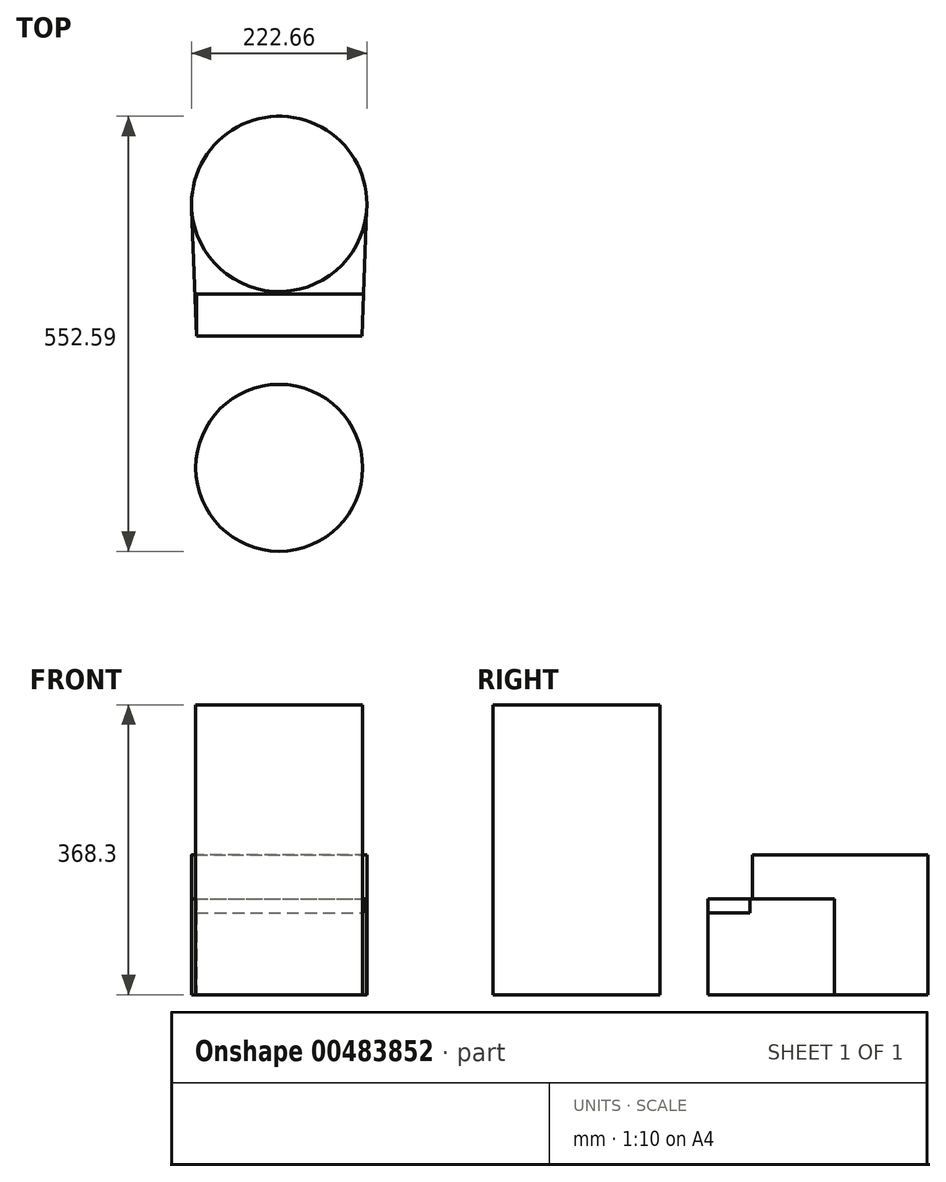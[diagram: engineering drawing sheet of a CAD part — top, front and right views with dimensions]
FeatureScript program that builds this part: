
annotation { "Feature Type Name" : "Feature", "Feature Type Description" : "" }
export const myFeature = defineFeature(function(context is Context, id is Id, definition is map)
    precondition{}
    {
        {
            var Q0;
            Q0=qCreatedBy(makeId("Top.planeOp"),FACE);
            var sketch = newSketch(context, id + "F0", { "sketchPlane" : qUnion([Q0])});
            skCircle(sketch, "E0", {"center": v(0, 168.12) * mm, "radius": 111.33 * mm});
            skCircle(sketch, "E1", {"center": v(0, -167.11) * mm, "radius": 106.03 * mm});
            skLineSegment(sketch, "E2", {"start": v(-111.1, 160.8) * mm, "end": v(-100.24, -132.56) * mm});
            skLineSegment(sketch, "E3", {"start": v(-111.1, 160.8) * mm, "end": v(111.1, 160.8) * mm});
            skLineSegment(sketch, "E4", {"start": v(111.1, 160.8) * mm, "end": v(100.24, -132.56) * mm});
            skLineSegment(sketch, "E5", {"start": v(-100.24, -132.56) * mm, "end": v(100.24, -132.56) * mm});
            skLineSegment(sketch, "E6", {"start": v(0, 168.12) * mm, "end": v(0, -167.11) * mm});
            skLineSegment(sketch, "E7", {"start": v(-63.13, 259.82) * mm, "end": v(0, 168.12) * mm});
            skLineSegment(sketch, "E8", {"start": v(-63.13, 259.82) * mm, "end": v(63.13, 259.82) * mm});
            skLineSegment(sketch, "E9", {"start": v(63.13, 259.82) * mm, "end": v(0, 168.12) * mm});
            skLineSegment(sketch, "E10", {"start": v(0, -167.11) * mm, "end": v(-63.13, -252.3) * mm});
            skLineSegment(sketch, "E11", {"start": v(-63.13, -252.3) * mm, "end": v(63.13, -252.3) * mm});
            skLineSegment(sketch, "E12", {"start": v(63.13, -252.3) * mm, "end": v(0, -167.11) * mm});
            skLineSegment(sketch, "E13", {"start": v(-111.1, 160.8) * mm, "end": v(0, 56.8) * mm});
            skLineSegment(sketch, "E14", {"start": v(0, 56.8) * mm, "end": v(111.1, 160.8) * mm});
            skLineSegment(sketch, "E15", {"start": v(-100.24, -132.56) * mm, "end": v(0, -61.08) * mm});
            skLineSegment(sketch, "E16", {"start": v(0, -61.08) * mm, "end": v(100.24, -132.56) * mm});
            skLineSegment(sketch, "E17", {"start": v(-105.14, 0) * mm, "end": v(105.14, 0) * mm});
            skLineSegment(sketch, "E18.bottom", {"start": v(-105.14, 0) * mm, "end": v(107.13, 0) * mm});
            skLineSegment(sketch, "E18.top", {"start": v(-105.14, 53.74) * mm, "end": v(107.13, 53.74) * mm});
            skLineSegment(sketch, "E18.left", {"start": v(-105.14, 0) * mm, "end": v(-105.14, 53.74) * mm});
            skLineSegment(sketch, "E18.right", {"start": v(107.13, 0) * mm, "end": v(107.13, 53.74) * mm});
            skSolve(sketch);
        }
        {
            var Q0;
            Q0=makeQuery(id+"F0.imprint","IMPRINT",FACE,{"disambiguationData":[TD([[makeQuery(id+"F0.imprint","IMPRINT",EDGE,{"derivedFrom":sQuery(id+"F0.wireOp",EDGE,"E10")}),1.0]])]});
            var Q1;
            {var subQ3=sQuery(id+"F0.wireOp",EDGE,"E12");Q1=makeQuery(id+"F0.imprint","IMPRINT",FACE,{"disambiguationData":[TD([[makeQuery(id+"F0.imprint","IMPRINT",EDGE,{"derivedFrom":subQ3}),-1.0]])]});}
            var Q2;
            {var subQ3=sQuery(id+"F0.wireOp",EDGE,"E10");Q2=makeQuery(id+"F0.imprint","IMPRINT",FACE,{"disambiguationData":[TD([[makeQuery(id+"F0.imprint","IMPRINT",EDGE,{"derivedFrom":subQ3}),-1.0]])]});}
            var Q3;
            {var subQ0=sQuery(id+"F0.wireOp",EDGE,"E15");Q3=makeQuery(id+"F0.imprint","IMPRINT",FACE,{"disambiguationData":[TD([[makeQuery(id+"F0.imprint","IMPRINT",EDGE,{"derivedFrom":subQ0}),-1.0]])]});}
            var Q4;
            {var subQ0=sQuery(id+"F0.wireOp",EDGE,"E16");Q4=makeQuery(id+"F0.imprint","IMPRINT",FACE,{"disambiguationData":[TD([[makeQuery(id+"F0.imprint","IMPRINT",EDGE,{"derivedFrom":subQ0}),-1.0]])]});}
            var Q5;
            {var subQ0=sQuery(id+"F0.wireOp",EDGE,"E11");Q5=makeQuery(id+"F0.imprint","IMPRINT",FACE,{"disambiguationData":[TD([[makeQuery(id+"F0.imprint","IMPRINT",EDGE,{"derivedFrom":subQ0}),-1.0]])]});}
            var Q6;
            {var subQ0=sQuery(id+"F0.wireOp",EDGE,"E15");Q6=makeQuery(id+"F0.imprint","IMPRINT",FACE,{"disambiguationData":[TD([[makeQuery(id+"F0.imprint","IMPRINT",EDGE,{"derivedFrom":subQ0}),1.0]])]});}
            var Q7;
            {var subQ0=sQuery(id+"F0.wireOp",EDGE,"E16");Q7=makeQuery(id+"F0.imprint","IMPRINT",FACE,{"disambiguationData":[TD([[makeQuery(id+"F0.imprint","IMPRINT",EDGE,{"derivedFrom":subQ0}),1.0]])]});}
            extrude(context, id + "F1", {"entities" : qUnion([Q0, Q1, Q2, Q3, Q4, Q5, Q6, Q7]), "depth" : 368.3 * mm});
        }
        {
            var Q0;
            {var subQ4=sQuery(id+"F0.wireOp",EDGE,"E6");var subQ6=sQuery(id+"F0.wireOp",EDGE,"E18.bottom");var subQ8=makeQuery(id+"F0.imprint","INTERSECT",VERTEX,{"derivedFrom":[subQ4,subQ6]});Q0=makeQuery(id+"F0.imprint","IMPRINT",FACE,{"disambiguationData":[TD([[makeQuery(id+"F0.imprint","IMPRINT",EDGE,{"disambiguationData":[TD([[subQ8,1.0]])],"derivedFrom":subQ6}),-1.0]])]});}
            var Q1;
            {var subQ1=sQuery(id+"F0.wireOp",EDGE,"E4");var subQ6=sQuery(id+"F0.wireOp",EDGE,"E18.bottom");var subQ7=makeQuery(id+"F0.imprint","INTERSECT",VERTEX,{"derivedFrom":[subQ1,subQ6]});Q1=makeQuery(id+"F0.imprint","IMPRINT",FACE,{"disambiguationData":[TD([[makeQuery(id+"F0.imprint","IMPRINT",EDGE,{"disambiguationData":[TD([[subQ7,1.0]])],"derivedFrom":subQ6}),-1.0]])]});}
            var Q2;
            {var subQ0=sQuery(id+"F0.wireOp",EDGE,"E18.top");var subQ5=sQuery(id+"F0.wireOp",EDGE,"E6");var subQ6=makeQuery(id+"F0.imprint","INTERSECT",VERTEX,{"derivedFrom":[subQ5,subQ0]});Q2=makeQuery(id+"F0.imprint","IMPRINT",FACE,{"disambiguationData":[TD([[makeQuery(id+"F0.imprint","IMPRINT",EDGE,{"disambiguationData":[TD([[subQ6,-1.0]])],"derivedFrom":subQ5}),1.0]])]});}
            var Q3;
            {var subQ5=sQuery(id+"F0.wireOp",EDGE,"E18.left");Q3=makeQuery(id+"F0.imprint","IMPRINT",FACE,{"disambiguationData":[TD([[makeQuery(id+"F0.imprint","IMPRINT",EDGE,{"derivedFrom":subQ5}),-1.0]])]});}
            extrude(context, id + "F2", {"entities" : qUnion([Q0, Q1, Q2, Q3]), "operationType" : NewBodyOperationType.ADD, "depth" : 104.14 * mm});
        }
        {
            var Q0;
            {var subQ0=sQuery(id+"F0.wireOp",EDGE,"E18.left");Q0=makeQuery(id+"F0.imprint","IMPRINT",FACE,{"disambiguationData":[TD([[makeQuery(id+"F0.imprint","IMPRINT",EDGE,{"derivedFrom":subQ0}),1.0]])]});}
            var Q1;
            {var subQ4=sQuery(id+"F0.wireOp",EDGE,"E6");var subQ6=sQuery(id+"F0.wireOp",EDGE,"E18.top");var subQ8=makeQuery(id+"F0.imprint","INTERSECT",VERTEX,{"derivedFrom":[subQ4,subQ6]});Q1=makeQuery(id+"F0.imprint","IMPRINT",FACE,{"disambiguationData":[TD([[makeQuery(id+"F0.imprint","IMPRINT",EDGE,{"disambiguationData":[TD([[subQ8,-1.0]])],"derivedFrom":subQ6}),1.0]])]});}
            extrude(context, id + "F3", {"entities" : qUnion([Q0, Q1]), "operationType" : NewBodyOperationType.ADD, "depth" : 121.92 * mm});
        }
        {
            var Q0;
            {var subQ0=sQuery(id+"F0.wireOp",EDGE,"E14");Q0=makeQuery(id+"F0.imprint","IMPRINT",FACE,{"disambiguationData":[TD([[makeQuery(id+"F0.imprint","IMPRINT",EDGE,{"derivedFrom":subQ0}),-1.0]])]});}
            var Q1;
            {var subQ0=sQuery(id+"F0.wireOp",EDGE,"E14");Q1=makeQuery(id+"F0.imprint","IMPRINT",FACE,{"disambiguationData":[TD([[makeQuery(id+"F0.imprint","IMPRINT",EDGE,{"derivedFrom":subQ0}),1.0]])]});}
            var Q2;
            {var subQ0=sQuery(id+"F0.wireOp",EDGE,"E13");Q2=makeQuery(id+"F0.imprint","IMPRINT",FACE,{"disambiguationData":[TD([[makeQuery(id+"F0.imprint","IMPRINT",EDGE,{"derivedFrom":subQ0}),-1.0]])]});}
            var Q3;
            {var subQ3=sQuery(id+"F0.wireOp",EDGE,"E7");Q3=makeQuery(id+"F0.imprint","IMPRINT",FACE,{"disambiguationData":[TD([[makeQuery(id+"F0.imprint","IMPRINT",EDGE,{"derivedFrom":subQ3}),-1.0]])]});}
            var Q4;
            {var subQ0=sQuery(id+"F0.wireOp",EDGE,"E13");Q4=makeQuery(id+"F0.imprint","IMPRINT",FACE,{"disambiguationData":[TD([[makeQuery(id+"F0.imprint","IMPRINT",EDGE,{"derivedFrom":subQ0}),1.0]])]});}
            var Q5;
            {var subQ0=sQuery(id+"F0.wireOp",EDGE,"E8");Q5=makeQuery(id+"F0.imprint","IMPRINT",FACE,{"disambiguationData":[TD([[makeQuery(id+"F0.imprint","IMPRINT",EDGE,{"derivedFrom":subQ0}),1.0]])]});}
            var Q6;
            {var subQ3=sQuery(id+"F0.wireOp",EDGE,"E9");Q6=makeQuery(id+"F0.imprint","IMPRINT",FACE,{"disambiguationData":[TD([[makeQuery(id+"F0.imprint","IMPRINT",EDGE,{"derivedFrom":subQ3}),1.0]])]});}
            var Q7;
            Q7=makeQuery(id+"F0.imprint","IMPRINT",FACE,{"disambiguationData":[TD([[makeQuery(id+"F0.imprint","IMPRINT",EDGE,{"derivedFrom":sQuery(id+"F0.wireOp",EDGE,"E7")}),1.0]])]});
            extrude(context, id + "F4", {"entities" : qUnion([Q0, Q1, Q2, Q3, Q4, Q5, Q6, Q7]), "operationType" : NewBodyOperationType.ADD, "depth" : 177.8 * mm});
        }
    });
